# Revit family: ASF-20-C6
name_source: partatom
category: Mechanical Equipment
units: mm (PartAtom-declared; Revit-internal decimal feet)

## family parameters
Always vertical = Yes
Classification = None
Cut with Voids When Loaded = No
Maintain Annotation Orientation = No
OmniClass Number = 23.75.00.00
OmniClass Title = Climate Control (HVAC)
Part Type = Normal
Room Calculation Point = No
Round Connector Dimension = Use Diameter
Shared = No
Work Plane-Based = No

## types (1)
- Standard
    Area = 72.45 SF
    Center of Gravity = X: 0.021 in Y: -5.975 in Z: -0.060 in
    Connector_1_Diameter = 1' - 7 3/4"
    Default Elevation = 0' - 0"
    Density = 123.01 lb/ft³
    Design State = 1
    Designer = CAD Machine
    Mass = 14.61 lbm
    Part Number = ASF-20-C6
    Requested Accuracy = Low
    Subject = ASF-20-C6
    Title = Aura Solar Attic Fan - 20" Diameter, 6" Tall Collar
    Volume = 0.12 CF

## geometry (parser evidence)
native form markers: Sweep x3
no freeform markers — native parametric forms only
